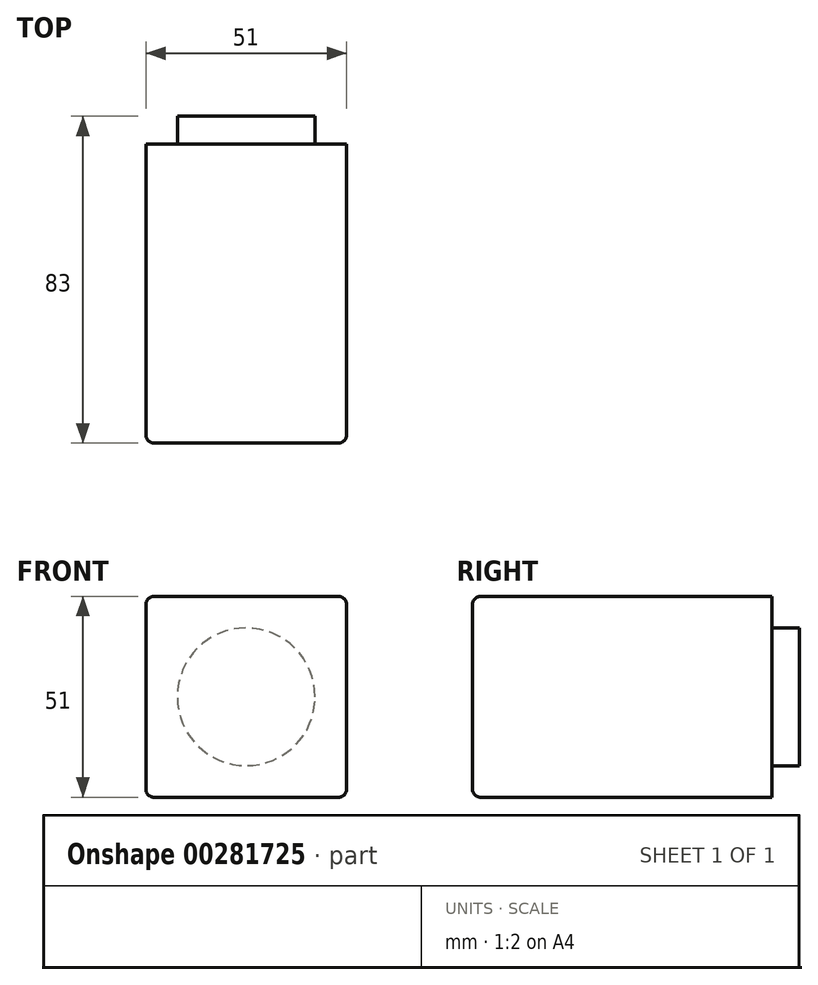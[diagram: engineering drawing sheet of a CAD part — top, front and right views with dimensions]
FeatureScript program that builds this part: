
annotation { "Feature Type Name" : "Feature", "Feature Type Description" : "" }
export const myFeature = defineFeature(function(context is Context, id is Id, definition is map)
    precondition{}
    {
        {
            var Q0;
            Q0=qCreatedBy(makeId("Front.planeOp"),FACE);
            var sketch = newSketch(context, id + "F0", { "sketchPlane" : qUnion([Q0])});
            skLineSegment(sketch, "E0.bottom", {"start": v(-23.5, 25.5) * mm, "end": v(23.5, 25.5) * mm});
            skLineSegment(sketch, "E0.top", {"start": v(-23.5, -25.5) * mm, "end": v(23.5, -25.5) * mm});
            skLineSegment(sketch, "E0.left", {"start": v(-25.5, 23.5) * mm, "end": v(-25.5, -23.5) * mm});
            skLineSegment(sketch, "E0.right", {"start": v(25.5, 23.5) * mm, "end": v(25.5, -23.5) * mm});
            skPoint(sketch, "E0.middle", {"position": v(0, 0) * mm});
            skPoint(sketch, "E1.visualSharp", {"position": v(-25.5, 25.5) * mm});
            skArc(sketch, "E1.filletArc", {"start": v(-23.5, 25.5) * mm, "mid": v(-24.91, 24.91) * mm, "end": v(-25.5, 23.5) * mm});
            skPoint(sketch, "E2.visualSharp", {"position": v(-25.5, -25.5) * mm});
            skArc(sketch, "E2.filletArc", {"start": v(-25.5, -23.5) * mm, "mid": v(-24.91, -24.91) * mm, "end": v(-23.5, -25.5) * mm});
            skPoint(sketch, "E3.visualSharp", {"position": v(25.5, -25.5) * mm});
            skArc(sketch, "E3.filletArc", {"start": v(23.5, -25.5) * mm, "mid": v(24.91, -24.91) * mm, "end": v(25.5, -23.5) * mm});
            skPoint(sketch, "E4.visualSharp", {"position": v(25.5, 25.5) * mm});
            skArc(sketch, "E4.filletArc", {"start": v(25.5, 23.5) * mm, "mid": v(24.91, 24.91) * mm, "end": v(23.5, 25.5) * mm});
            skCircle(sketch, "E5", {"center": v(0, 0) * mm, "radius": 17.5 * mm});
            skSolve(sketch);
        }
        {
            var Q0;
            Q0=makeQuery(id+"F0.imprint","IMPRINT",FACE,{"disambiguationData":[TD([[makeQuery(id+"F0.imprint","IMPRINT",EDGE,{"derivedFrom":sQuery(id+"F0.wireOp",EDGE,"E0.bottom")}),-1.0]])]});
            var Q1;
            Q1=makeQuery(id+"F0.imprint","IMPRINT",FACE,{"disambiguationData":[TD([[makeQuery(id+"F0.imprint","IMPRINT",EDGE,{"derivedFrom":sQuery(id+"F0.wireOp",EDGE,"E5")}),1.0]])]});
            extrude(context, id + "F1", {"entities" : qUnion([Q0, Q1]), "depth" : 76 * mm, "offsetDistance" : 25 * mm});
        }
        {
            var Q0;
            Q0=makeQuery(id+"F0.imprint","IMPRINT",FACE,{"disambiguationData":[TD([[makeQuery(id+"F0.imprint","IMPRINT",EDGE,{"derivedFrom":sQuery(id+"F0.wireOp",EDGE,"E5")}),1.0]])]});
            extrude(context, id + "F2", {"entities" : qUnion([Q0]), "operationType" : NewBodyOperationType.ADD, "oppositeDirection" : true, "depth" : 7 * mm, "offsetDistance" : 25 * mm});
        }
        {
            var Q0;
            Q0=makeQuery(id+"F1.opExtrude","CAP_EDGE",EDGE,{"disambiguationData":[OSD([sQuery(id+"F0.wireOp",EDGE,"E0.right")])],"isStart":false});
            fillet(context, id + "F3", {"entities" : qUnion([Q0]), "radius" : 2 * mm, "tangentPropagation" : true, "allowEdgeOverflow" : false});
        }
    });
